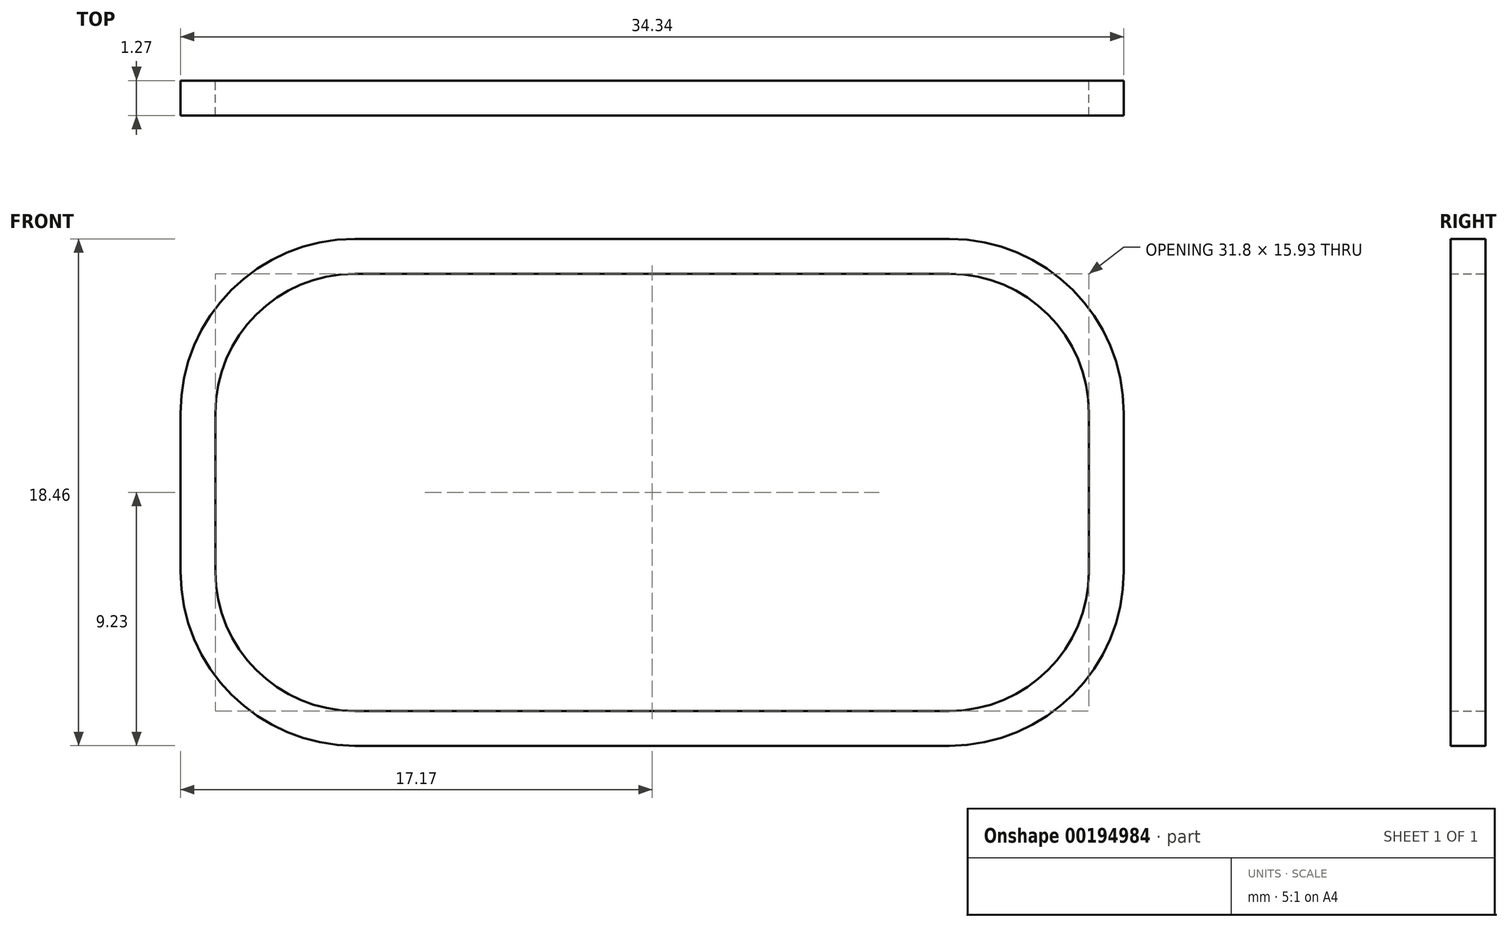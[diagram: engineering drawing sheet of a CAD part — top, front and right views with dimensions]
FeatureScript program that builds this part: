
annotation { "Feature Type Name" : "Feature", "Feature Type Description" : "" }
export const myFeature = defineFeature(function(context is Context, id is Id, definition is map)
    precondition{}
    {
        {
            var Q0;
            Q0=qCreatedBy(makeId("Front.planeOp"),FACE);
            var sketch = newSketch(context, id + "F0", { "sketchPlane" : qUnion([Q0])});
            skLineSegment(sketch, "E0.bottom", {"start": v(-10.82, -9.23) * mm, "end": v(10.82, -9.23) * mm});
            skLineSegment(sketch, "E0.top", {"start": v(-10.82, 9.23) * mm, "end": v(10.82, 9.23) * mm});
            skLineSegment(sketch, "E0.left", {"start": v(-17.17, -2.88) * mm, "end": v(-17.17, 2.88) * mm});
            skLineSegment(sketch, "E0.right", {"start": v(17.17, -2.88) * mm, "end": v(17.17, 2.88) * mm});
            skPoint(sketch, "E0.middle", {"position": v(0, 0) * mm});
            skPoint(sketch, "E1.visualSharp", {"position": v(-17.17, 9.23) * mm});
            skArc(sketch, "E1.filletArc", {"start": v(-10.82, 9.23) * mm, "mid": v(-15.31, 7.37) * mm, "end": v(-17.17, 2.88) * mm});
            skPoint(sketch, "E2.visualSharp", {"position": v(17.17, 9.23) * mm});
            skArc(sketch, "E2.filletArc", {"start": v(17.17, 2.88) * mm, "mid": v(15.31, 7.37) * mm, "end": v(10.82, 9.23) * mm});
            skPoint(sketch, "E3.visualSharp", {"position": v(17.17, -9.23) * mm});
            skArc(sketch, "E3.filletArc", {"start": v(10.82, -9.23) * mm, "mid": v(15.31, -7.37) * mm, "end": v(17.17, -2.88) * mm});
            skPoint(sketch, "E4.visualSharp", {"position": v(-17.17, -9.23) * mm});
            skArc(sketch, "E4.filletArc", {"start": v(-17.17, -2.88) * mm, "mid": v(-15.31, -7.37) * mm, "end": v(-10.82, -9.23) * mm});
            skArc(sketch, "E5.0", {"start": v(-15.9, -2.88) * mm, "mid": v(-14.41, -6.48) * mm, "end": v(-10.82, -7.96) * mm});
            skLineSegment(sketch, "E5.1", {"start": v(-10.82, -7.96) * mm, "end": v(10.82, -7.96) * mm});
            skLineSegment(sketch, "E5.2", {"start": v(-15.9, -2.88) * mm, "end": v(-15.9, 2.88) * mm});
            skArc(sketch, "E5.3", {"start": v(10.82, -7.96) * mm, "mid": v(14.41, -6.48) * mm, "end": v(15.9, -2.88) * mm});
            skArc(sketch, "E5.4", {"start": v(-10.82, 7.96) * mm, "mid": v(-14.41, 6.48) * mm, "end": v(-15.9, 2.88) * mm});
            skLineSegment(sketch, "E5.5", {"start": v(-10.82, 7.96) * mm, "end": v(10.82, 7.96) * mm});
            skArc(sketch, "E5.6", {"start": v(15.9, 2.88) * mm, "mid": v(14.41, 6.48) * mm, "end": v(10.82, 7.96) * mm});
            skLineSegment(sketch, "E5.7", {"start": v(15.9, -2.88) * mm, "end": v(15.9, 2.88) * mm});
            skSolve(sketch);
        }
        {
            var Q0;
            Q0=makeQuery(id+"F0.imprint","IMPRINT",FACE,{"disambiguationData":[TD([[makeQuery(id+"F0.imprint","IMPRINT",EDGE,{"derivedFrom":sQuery(id+"F0.wireOp",EDGE,"E0.bottom")}),1.0]])]});
            extrude(context, id + "F1", {"entities" : qUnion([Q0]), "depth" : 1.27 * mm});
        }
    });
